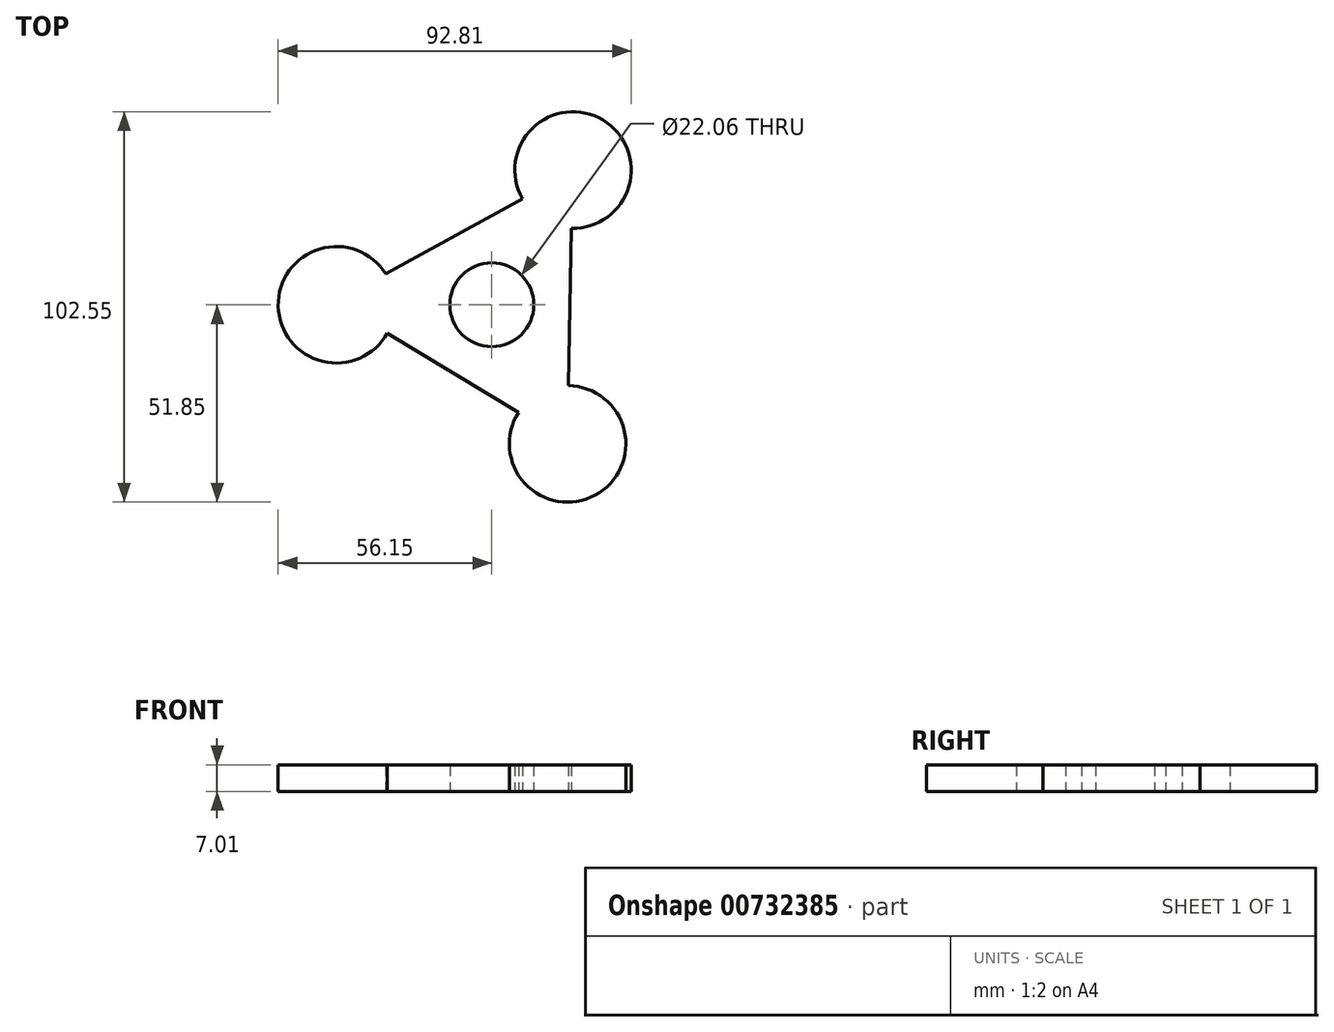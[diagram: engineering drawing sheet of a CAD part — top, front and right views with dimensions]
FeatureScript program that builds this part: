
annotation { "Feature Type Name" : "Feature", "Feature Type Description" : "" }
export const myFeature = defineFeature(function(context is Context, id is Id, definition is map)
    precondition{}
    {
        {
            var Q0;
            Q0=qCreatedBy(makeId("Top.planeOp"),FACE);
            var sketch = newSketch(context, id + "F0", { "sketchPlane" : qUnion([Q0])});
            skCircle(sketch, "E0.cCircle", {"center": v(0, 0) * mm, "radius": 20.55 * mm, "construction": true});
            skLineSegment(sketch, "E0.0", {"start": v(-41.09, 0.79) * mm, "end": v(21.23, 35.19) * mm});
            skLineSegment(sketch, "E0.1", {"start": v(21.23, 35.19) * mm, "end": v(19.86, -35.98) * mm});
            skLineSegment(sketch, "E0.2", {"start": v(19.86, -35.98) * mm, "end": v(-41.09, 0.79) * mm});
            skPoint(sketch, "E0.0.midPoint", {"position": v(-9.93, 17.99) * mm});
            skSolve(sketch);
        }
        {
            var Q0;
            Q0=qSketchRegion(id+"F0",true);
            extrude(context, id + "F1", {"entities" : qUnion([Q0]), "depth" : 7 * mm, "offsetDistance" : 25.4 * mm});
        }
        {
            var Q0;
            Q0=sQuery(id+"F0.wireOp",VERTEX,"E0.cCircle.center");
            var Q1;
            Q1=makeQuery(id+"F1.opExtrude","SWEPT_BODY",BODY,{"disambiguationData":[OSD([sQuery(id+"F0.wireOp",EDGE,"E0.0"),sQuery(id+"F0.wireOp",EDGE,"E0.1"),sQuery(id+"F0.wireOp",EDGE,"E0.2")])]});
            hole(context, id + "F2", {"style" : HoleStyle.SIMPLE, "endStyle" : HoleEndStyle.THROUGH, "oppositeDirection" : true, "holeDiameter" : 22.06 * mm, "majorDiameter" : 6.35 * mm, "isTappedThrough" : true, "tappedDepth" : 12.7 * mm, "tapClearance" : 3, "locations" : qUnion([Q0]), "scope" : qUnion([Q1])});
        }
        {
            var Q0;
            Q0=qCreatedBy(makeId("Top.planeOp"),FACE);
            var sketch = newSketch(context, id + "F3", { "sketchPlane" : qUnion([Q0])});
            skCircle(sketch, "E1", {"center": v(21.35, 35.4) * mm, "radius": 15.3 * mm});
            skCircle(sketch, "E2", {"center": v(-40.84, 0) * mm, "radius": 15.3 * mm});
            skCircle(sketch, "E3", {"center": v(19.92, -36.54) * mm, "radius": 15.3 * mm});
            skSolve(sketch);
        }
        {
            var Q0;
            Q0=qSketchRegion(id+"F3",true);
            extrude(context, id + "F4", {"entities" : qUnion([Q0]), "operationType" : NewBodyOperationType.ADD, "depth" : 7 * mm, "offsetDistance" : 25.4 * mm});
        }
    });
